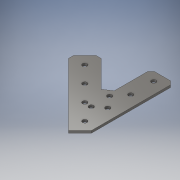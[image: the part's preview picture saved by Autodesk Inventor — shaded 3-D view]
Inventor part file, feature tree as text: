
AUTODESK INVENTOR PART (.ipt)
format: ipt  version: 2017 (Build 210142000, 142)  size: 120,832 bytes
history: native  units: in
note: dims shown in document units (in); Inventor stores cm internally (conversion verified against a paired STEP export)
features: extrude x1, sketch x1
ambient origin geometry x8: Origin, YZ Plane, XZ Plane, XY Plane, X Axis, Y Axis, Z Axis, Center Point
bodies: Solid1 (feature_tree)
feature tree (2):
  extrude  "Extrusion1"  TaperAngle=45.0deg  [1 undecoded]
  sketch  "Sketch1"  dims[d3=0.7in d4=45.0deg d37=0.1in d38=0.0in]
note: 1 required parameter value undecoded (feature->parameter linkage not recoverable at this tier; creation-order binding heuristic only, values carry confidence <= 0.55)
